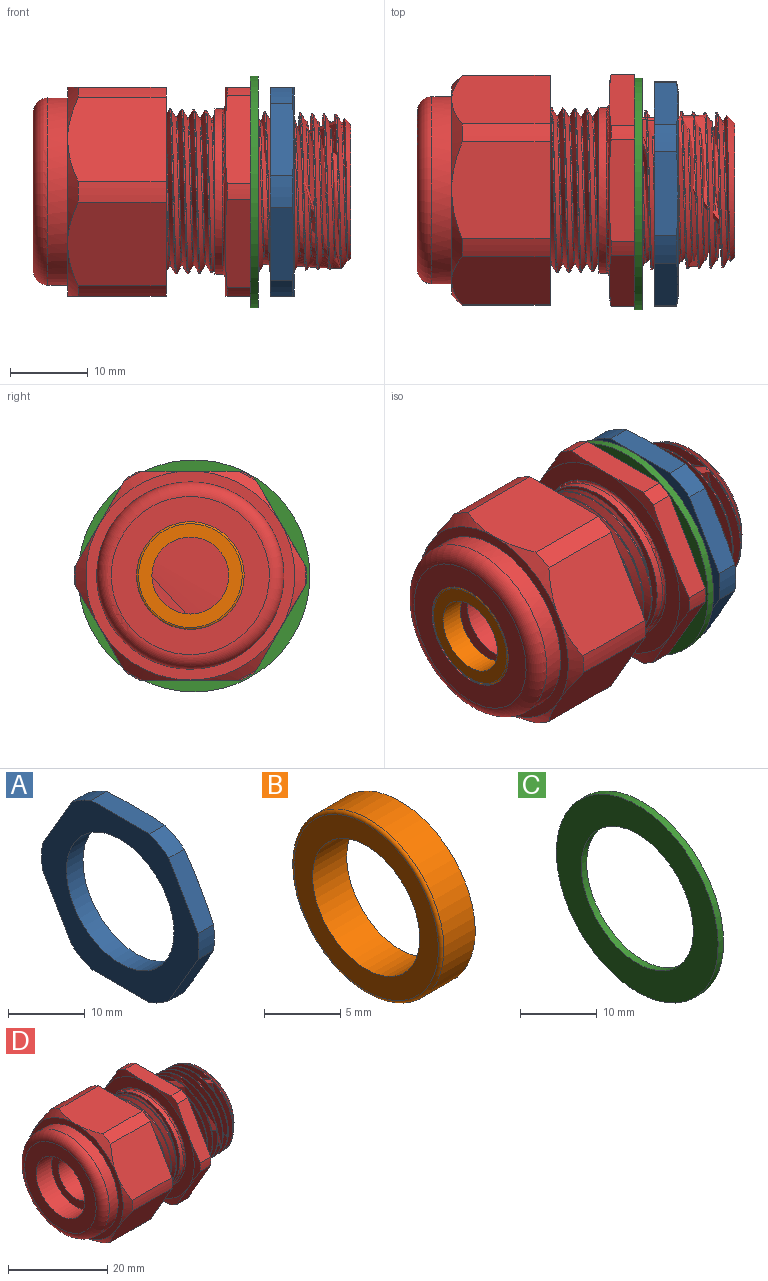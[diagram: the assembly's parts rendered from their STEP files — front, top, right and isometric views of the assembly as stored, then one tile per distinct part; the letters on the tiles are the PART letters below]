
ASSEMBLY  parts=4 mates=3
PART A: 21 faces, bbox 3.6x29.6x29.6 mm
  f0: plane 26.92x26.92mm, normal (1,0,0), area 259.7mm2, adj f14,f15,f16,f17,f18,f19,f20
  f1: cylinder r=14.5mm len=3.56mm, axis (-1,0,0), area 11.8mm2, adj f2,f12,f13,f15
  f2: plane 9.9x5.95mm, normal (0,0.87,-0.5), area 32.2mm2, adj f1,f3,f13,f15,f20
  f3: cylinder r=14.5mm len=4.12mm, axis (-1,0,0), area 11.8mm2, adj f2,f4,f13,f20
  f4: plane 9.9x5.95mm, normal (0,0.87,0.5), area 32.2mm2, adj f3,f5,f13,f19,f20
  f5: cylinder r=14.5mm len=3.56mm, axis (-1,0,0), area 11.8mm2, adj f4,f6,f13,f19
  f6: plane 11.35x3.6mm, normal (0,0,1), area 32.2mm2, adj f5,f7,f13,f18,f19
  f7: cylinder r=14.5mm len=3.56mm, axis (-1,0,0), area 11.8mm2, adj f6,f8,f13,f18
  f8: plane 9.9x5.95mm, normal (0,-0.87,0.5), area 32.2mm2, adj f7,f9,f13,f17,f18
  f9: cylinder r=14.5mm len=4.12mm, axis (-1,0,0), area 11.8mm2, adj f8,f10,f13,f17
  f10: plane 9.9x5.95mm, normal (0,-0.87,-0.5), area 32.2mm2, adj f9,f11,f13,f16,f17
  f11: cylinder r=14.5mm len=3.56mm, axis (-1,0,0), area 11.8mm2, adj f10,f12,f13,f16
  f12: plane 11.35x3.6mm, normal (0,0,-1), area 32.2mm2, adj f1,f11,f13,f15,f16
  f13: plane 29.01x26.92mm, normal (-1,0,0), area 305.9mm2, adj f1,f2,f3,f4,f5,f6,f7,f8
  f14: cylinder r=9.93mm len=19.86mm, axis (-1,0,0), area 190.1mm2, adj f0,f13
  f15: cone r=13.46mm half-angle=80deg, axis (-1,0,0), area 9.8mm2, adj f0,f1,f2,f12
  f16: cone r=13.46mm half-angle=80deg, axis (-1,0,0), area 9.8mm2, adj f0,f10,f11,f12
  f17: cone r=13.46mm half-angle=80deg, axis (-1,0,0), area 9.8mm2, adj f0,f8,f9,f10
  f18: cone r=13.46mm half-angle=80deg, axis (-1,0,0), area 9.8mm2, adj f0,f6,f7,f8
  f19: cone r=13.46mm half-angle=80deg, axis (-1,0,0), area 9.8mm2, adj f0,f4,f5,f6
  f20: cone r=13.46mm half-angle=80deg, axis (-1,0,0), area 9.8mm2, adj f0,f2,f3,f4
PART B: 5 faces, bbox 3.1x15x15 mm
  f0: cylinder r=6.93mm len=13.87mm, axis (1,0,0), area 126.2mm2, adj f1,f4
  f1: torus R=6.68mm, axis (1,0,0), area 17.2mm2, adj f0,f2
  f2: plane 13.36x13.36mm, normal (-1,0,0), area 63.1mm2, adj f1,f3
  f3: cylinder r=4.95mm len=9.91mm, axis (1,0,0), area 98mm2, adj f2,f4
  f4: plane 13.87x13.87mm, normal (1,0,0), area 74mm2, adj f0,f3
PART C: 4 faces, bbox 1x29.9x29.9 mm
  f0: cylinder r=14.94mm len=29.88mm, axis (1,0,0), area 95.4mm2, adj f1,f3
  f1: plane 29.88x29.88mm, normal (-1,0,0), area 364.4mm2, adj f0,f2
  f2: cylinder r=10.36mm len=20.71mm, axis (1,0,0), area 66.1mm2, adj f1,f3
  f3: plane 29.88x29.88mm, normal (1,0,0), area 364.4mm2, adj f0,f2
PART D: 67 faces, bbox 42.2x30.9x30.9 mm
  f0: cone r=10.43mm half-angle=1.8deg, axis (-1,0,0), area 46.8mm2, adj f4,f5,f6,f32
  f1: cone r=4.95mm half-angle=3deg, axis (1,0,0), area 202.4mm2, adj f24,f34
  f2: bspline ~19.15x19.11mm, area 47.2mm2, adj f3,f5,f6,f32
  f3: bspline ~21.43x21.37mm, area 297.5mm2, adj f2,f4,f6,f32
  f4: bspline ~21.47x21.4mm, area 13.7mm2, adj f0,f3,f6,f32
  f5: bspline ~21.49x21.45mm, area 298.4mm2, adj f0,f2,f6,f32
  f6: plane 30.25x27.52mm, normal (1,0,0), area 297.9mm2, adj f0,f2,f3,f4,f5,f8,f9,f10
  f7: plane 26.92x26.92mm, normal (-1,0,0), area 112mm2, adj f20,f26,f27,f28,f29,f30,f31
  f8: cylinder r=14.83mm len=11.33mm, axis (-1,0,0), area 30.6mm2, adj f6,f9,f19,f26
  f9: plane 13.7x11.76mm, normal (0,0.87,0.5), area 152.2mm2, adj f6,f8,f10,f26,f31
  f10: cylinder r=14.83mm len=11.33mm, axis (-1,0,0), area 30.6mm2, adj f6,f9,f11,f31
  f11: plane 13.69x13.43mm, normal (0,0,1), area 152.2mm2, adj f6,f10,f12,f30,f31
  f12: cylinder r=14.83mm len=11.33mm, axis (-1,0,0), area 30.6mm2, adj f6,f11,f13,f30
  f13: plane 13.7x11.76mm, normal (0,-0.87,0.5), area 152.2mm2, adj f6,f12,f14,f29,f30
  f14: cylinder r=14.83mm len=11.33mm, axis (-1,0,0), area 30.6mm2, adj f6,f13,f15,f29
  f15: plane 13.7x11.76mm, normal (0,-0.87,-0.5), area 152.2mm2, adj f6,f14,f16,f28,f29
  f16: cylinder r=14.83mm len=11.33mm, axis (-1,0,0), area 30.6mm2, adj f6,f15,f17,f28
  f17: plane 13.69x13.43mm, normal (0,0,-1), area 152.2mm2, adj f6,f16,f18,f27,f28
  f18: cylinder r=14.83mm len=11.33mm, axis (-1,0,0), area 30.6mm2, adj f6,f17,f19,f27
  f19: plane 13.7x11.76mm, normal (0,0.87,-0.5), area 152.2mm2, adj f6,f8,f18,f26,f27
  f20: cylinder r=12.06mm len=24.13mm, axis (1,0,0), area 192.5mm2, adj f7,f25
  f21: plane 20.37x20.37mm, normal (-1,0,0), area 174.9mm2, adj f22,f25
  f22: cylinder r=6.93mm len=13.87mm, axis (1,0,0), area 192.6mm2, adj f21,f23
  f23: plane 13.87x13.87mm, normal (-1,0,0), area 74mm2, adj f22,f24
  f24: cylinder r=4.95mm len=12.7mm, axis (1,0,0), area 395.2mm2, adj f1,f23
  f25: torus R=10.19mm, axis (-1,0,0), area 211.1mm2, adj f20,f21
  f26: cone r=13.46mm half-angle=45deg, axis (1,0,0), area 16.6mm2, adj f7,f8,f9,f19
  f27: cone r=13.46mm half-angle=45deg, axis (1,0,0), area 16.6mm2, adj f7,f17,f18,f19
  f28: cone r=13.46mm half-angle=45deg, axis (1,0,0), area 16.6mm2, adj f7,f15,f16,f17
  f29: cone r=13.46mm half-angle=45deg, axis (1,0,0), area 16.6mm2, adj f7,f13,f14,f15
  f30: cone r=13.46mm half-angle=45deg, axis (1,0,0), area 16.6mm2, adj f7,f11,f12,f13
  f31: cone r=13.46mm half-angle=45deg, axis (1,0,0), area 16.6mm2, adj f7,f9,f10,f11
  f32: plane 21.93x21.93mm, normal (-1,0,0), area 45.6mm2, adj f0,f2,f3,f4,f5,f33
  f33: cylinder r=10.67mm len=21.34mm, axis (1,0,0), area 65.1mm2, adj f32,f66
  f34: plane 10.57x10.57mm, normal (-1,0,0), area 10.6mm2, adj f1,f36
  f35: plane 11.04x11.04mm, normal (1,0,0), area 18.7mm2, adj f36,f65
  f36: cylinder r=4.95mm len=9.91mm, axis (1,0,0), area 141.1mm2, adj f34,f35
  f37: cylinder r=14.98mm len=2.97mm, axis (-1,0,0), area 6.2mm2, adj f38,f50,f55,f56
  f38: plane 13.95x4.05mm, normal (0,0,-1), area 41.3mm2, adj f37,f39,f49,f50,f56
  f39: cylinder r=14.98mm len=2.97mm, axis (-1,0,0), area 6.2mm2, adj f38,f40,f49,f56
  f40: plane 12.19x7.38mm, normal (0,-0.87,-0.5), area 41.3mm2, adj f39,f41,f48,f49,f56
  f41: cylinder r=14.98mm len=2.97mm, axis (-1,0,0), area 6.2mm2, adj f40,f42,f48,f56
  f42: plane 12.19x7.38mm, normal (0,-0.87,0.5), area 41.3mm2, adj f41,f43,f48,f53,f56
  f43: cylinder r=14.98mm len=2.97mm, axis (-1,0,0), area 6.2mm2, adj f42,f44,f53,f56
  f44: plane 13.95x4.05mm, normal (0,0,1), area 41.3mm2, adj f43,f45,f52,f53,f56
  f45: cylinder r=14.98mm len=2.97mm, axis (-1,0,0), area 6.2mm2, adj f44,f46,f52,f56
  f46: plane 12.19x7.38mm, normal (0,0.87,0.5), area 41.3mm2, adj f45,f47,f51,f52,f56
  f47: cylinder r=14.98mm len=2.97mm, axis (-1,0,0), area 6.2mm2, adj f46,f51,f55,f56
  f48: cone r=13.46mm half-angle=80deg, axis (1,0,0), area 12.8mm2, adj f40,f41,f42,f54
  f49: cone r=13.46mm half-angle=80deg, axis (1,0,0), area 12.8mm2, adj f38,f39,f40,f54
  f50: cone r=13.46mm half-angle=80deg, axis (1,0,0), area 12.8mm2, adj f37,f38,f54,f55
  f51: cone r=13.46mm half-angle=80deg, axis (1,0,0), area 12.8mm2, adj f46,f47,f54,f55
  f52: cone r=13.46mm half-angle=80deg, axis (1,0,0), area 12.8mm2, adj f44,f45,f46,f54
  f53: cone r=13.46mm half-angle=80deg, axis (1,0,0), area 12.8mm2, adj f42,f43,f44,f54
  f54: plane 26.92x26.92mm, normal (-1,0,0), area 189.8mm2, adj f48,f49,f50,f51,f52,f53,f66
  f55: plane 12.19x7.38mm, normal (0,0.87,-0.5), area 41.3mm2, adj f37,f47,f50,f51,f56
  f56: plane 30.54x27.51mm, normal (1,0,0), area 321.2mm2, adj f37,f38,f39,f40,f41,f42,f43,f44
  f57: cone r=8.62mm half-angle=46.8deg, axis (-1,0,0), area 10.1mm2, adj f58,f59,f60,f61,f62
  f58: cone r=8.62mm half-angle=46.8deg, axis (-1,0,0), area 54.4mm2, adj f57,f59,f63,f64
  f59: bspline ~20.84x20.79mm, area 552.2mm2, adj f56,f57,f58,f60,f63
  f60: cone r=9.93mm half-angle=1.8deg, axis (-1,0,0), area 91.7mm2, adj f56,f57,f59,f61
  f61: bspline ~20.8x20.8mm, area 24.5mm2, adj f56,f57,f60,f62
  f62: bspline ~20.73x20.7mm, area 552.2mm2, adj f56,f57,f61,f63
  f63: bspline ~18.45x18.22mm, area 90.7mm2, adj f56,f58,f59,f62
  f64: plane 17.23x17.23mm, normal (1,0,0), area 112.5mm2, adj f58,f65
  f65: cone r=4.95mm half-angle=3deg, axis (1,0,0), area 477.6mm2, adj f35,f64
  f66: torus R=10.99mm, axis (-1,0,0), area 34.5mm2, adj f33,f54
PLACE A t=(7.6,0,0)mm
PLACE B t=(6.77,0.47,0.04)mm
PLACE C t=(6.98,0,0)mm
PLACE D t=(7.54,0.47,0.04)mm
MATE fastened D.f35 <-> C.f0  axis (1,0,0) through (-0.34,0,0)mm
MATE fastened C.f0 <-> A.f1  axis (1,0,0) through (0.68,0,0)mm
MATE fastened B.f0 <-> D.f0  axis (-1,0,0) through (-28.28,0.47,0.04)mm
